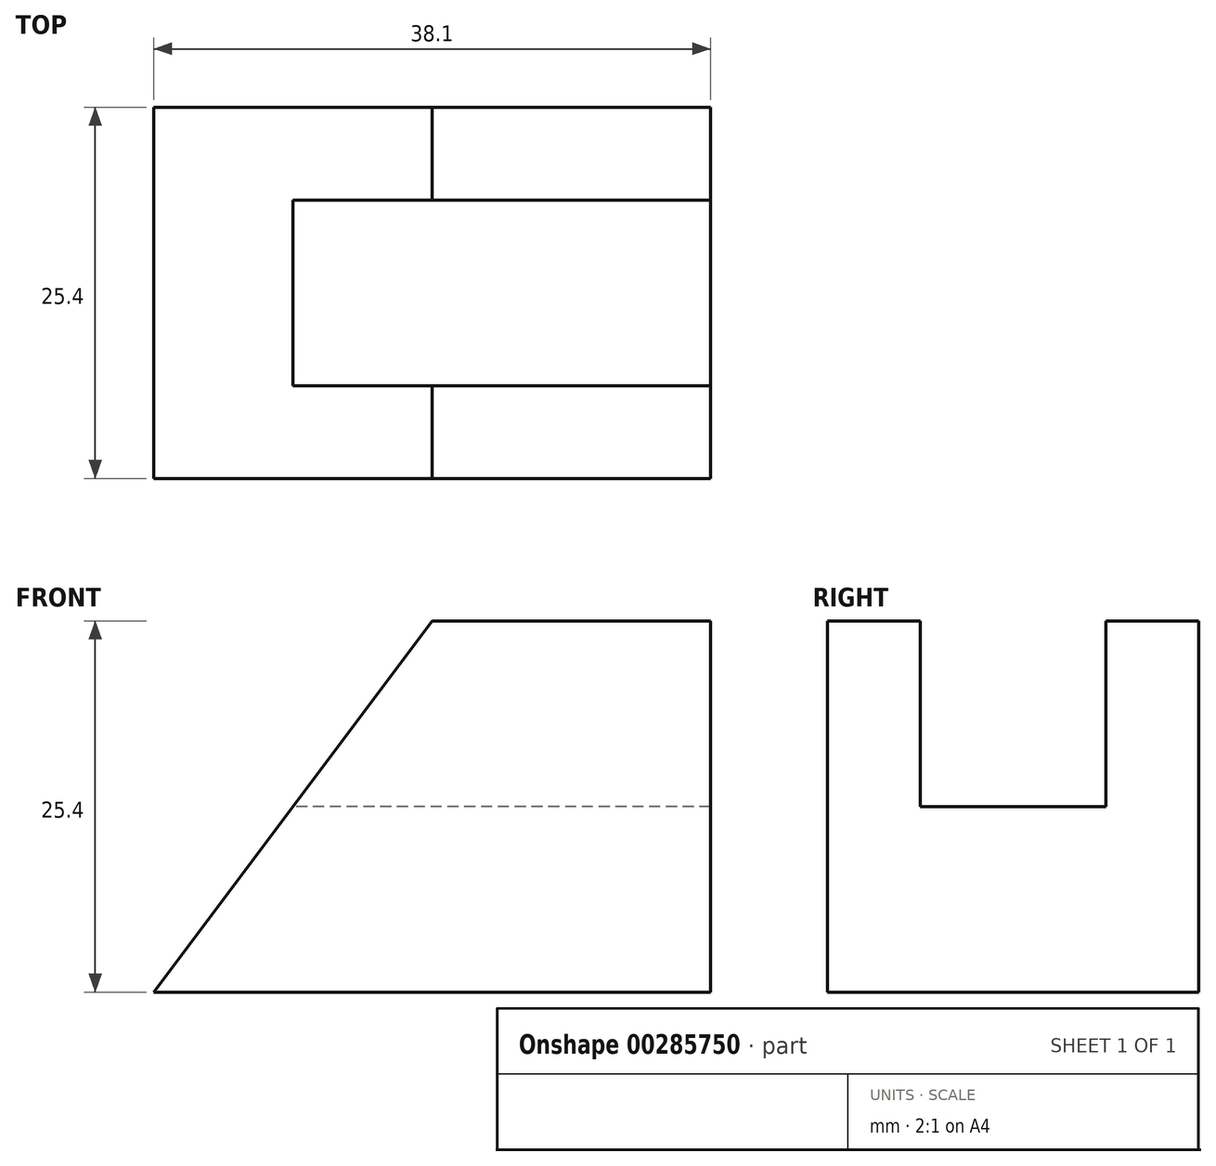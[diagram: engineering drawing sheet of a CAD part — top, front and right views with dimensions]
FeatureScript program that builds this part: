
annotation { "Feature Type Name" : "Feature", "Feature Type Description" : "" }
export const myFeature = defineFeature(function(context is Context, id is Id, definition is map)
    precondition{}
    {
        {
            var Q0;
            Q0=qCreatedBy(makeId("Front.planeOp"),FACE);
            var sketch = newSketch(context, id + "F0", { "sketchPlane" : qUnion([Q0])});
            skLineSegment(sketch, "E0", {"start": v(0, 0) * mm, "end": v(0, 12.7) * mm});
            skLineSegment(sketch, "E1", {"start": v(0, 12.7) * mm, "end": v(-28.58, 12.7) * mm});
            skLineSegment(sketch, "E2", {"start": v(0, 0) * mm, "end": v(-38.1, 0) * mm});
            skLineSegment(sketch, "E3", {"start": v(-38.1, 0) * mm, "end": v(-28.58, 12.7) * mm});
            skSolve(sketch);
        }
        {
            var Q0;
            Q0 = qSketchRegion(id + "F0", true);
            extrude(context, id + "F1", {"entities" : qUnion([Q0]), "depth" : 12.7 * mm});
        }
        {
            var Q0;
            Q0=makeQuery(id+"F1.opExtrude","CAP_FACE",FACE,{"disambiguationData":[OSD([sQuery(id+"F0.wireOp",EDGE,"E0"),sQuery(id+"F0.wireOp",EDGE,"E1"),sQuery(id+"F0.wireOp",EDGE,"E2"),sQuery(id+"F0.wireOp",EDGE,"E3")])],"isStart":false});
            var sketch = newSketch(context, id + "F2", { "sketchPlane" : qUnion([Q0])});
            skLineSegment(sketch, "E4", {"start": v(-38.1, 0) * mm, "end": v(0, 0) * mm});
            skLineSegment(sketch, "E5", {"start": v(0, 0) * mm, "end": v(0, 25.4) * mm});
            skLineSegment(sketch, "E6", {"start": v(0, 25.4) * mm, "end": v(-19.05, 25.4) * mm});
            skLineSegment(sketch, "E7", {"start": v(-19.05, 25.4) * mm, "end": v(-38.1, 0) * mm});
            skSolve(sketch);
        }
        {
            var Q0;
            Q0 = qSketchRegion(id + "F2", true);
            extrude(context, id + "F3", {"entities" : qUnion([Q0]), "operationType" : NewBodyOperationType.ADD, "depth" : 6.35 * mm});
        }
        {
            var Q0;
            Q0=makeQuery(id+"F1.opExtrude","CAP_FACE",FACE,{"disambiguationData":[OSD([sQuery(id+"F0.wireOp",EDGE,"E0"),sQuery(id+"F0.wireOp",EDGE,"E1"),sQuery(id+"F0.wireOp",EDGE,"E2"),sQuery(id+"F0.wireOp",EDGE,"E3")])],"isStart":true});
            var sketch = newSketch(context, id + "F4", { "sketchPlane" : qUnion([Q0])});
            skLineSegment(sketch, "E8", {"start": v(38.1, 0) * mm, "end": v(0, 0) * mm});
            skLineSegment(sketch, "E9", {"start": v(0, 0) * mm, "end": v(0, 25.4) * mm});
            skLineSegment(sketch, "E10", {"start": v(0, 25.4) * mm, "end": v(19.05, 25.4) * mm});
            skLineSegment(sketch, "E11", {"start": v(19.05, 25.4) * mm, "end": v(38.1, 0) * mm});
            skSolve(sketch);
        }
        {
            var Q0;
            Q0 = qSketchRegion(id + "F4", true);
            extrude(context, id + "F5", {"entities" : qUnion([Q0]), "operationType" : NewBodyOperationType.ADD, "depth" : 6.35 * mm});
        }
    });
